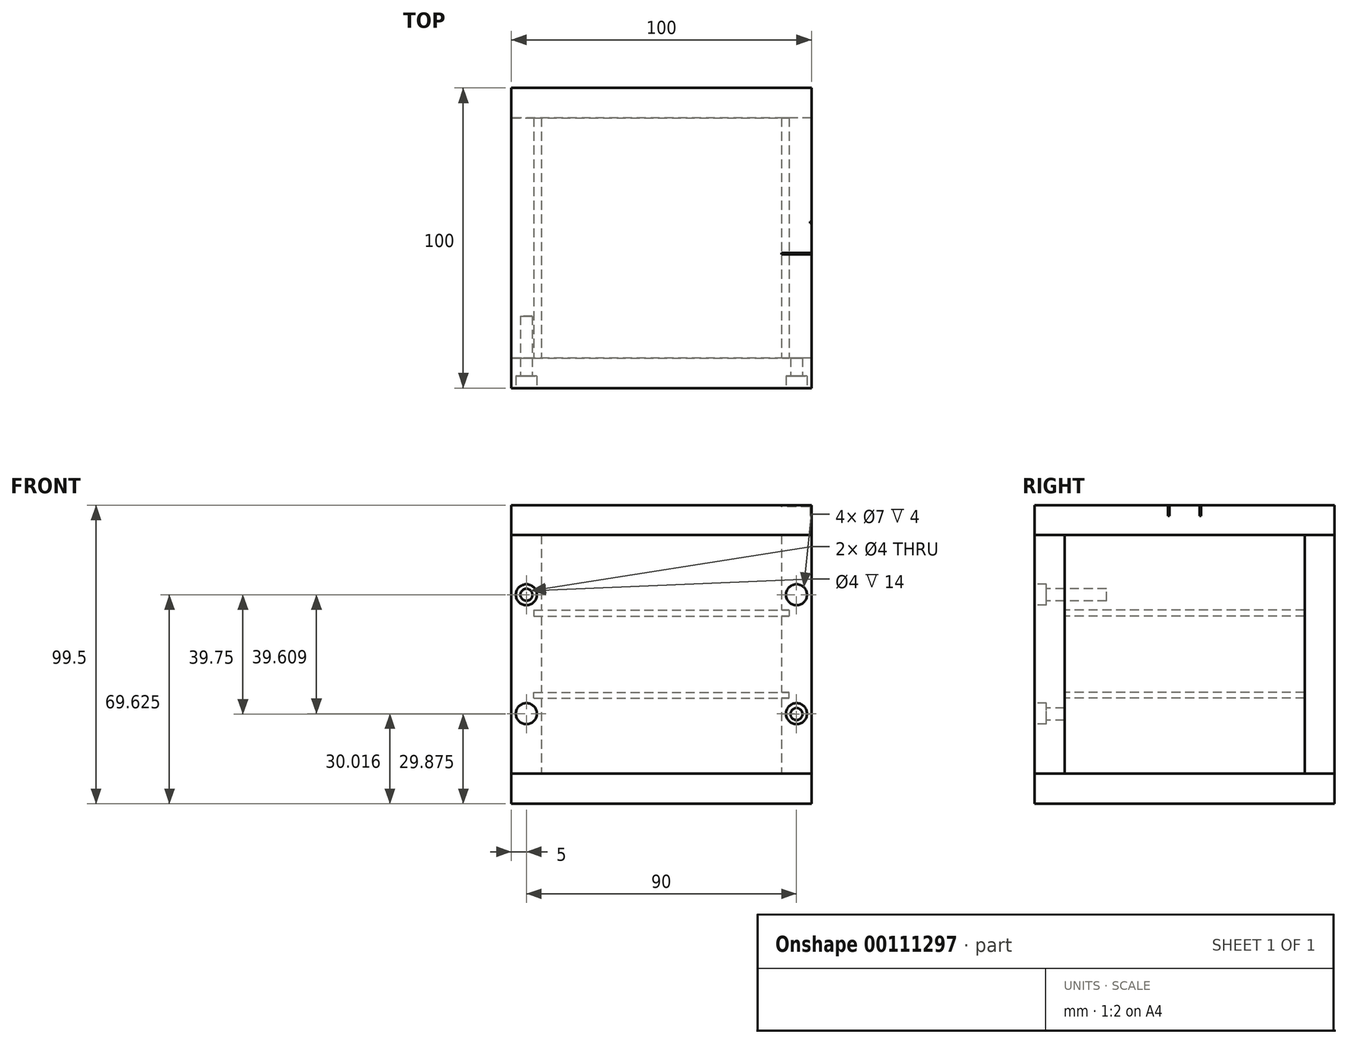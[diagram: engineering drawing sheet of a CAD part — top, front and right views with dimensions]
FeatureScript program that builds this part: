
annotation { "Feature Type Name" : "Feature", "Feature Type Description" : "" }
export const myFeature = defineFeature(function(context is Context, id is Id, definition is map)
    precondition{}
    {
        {
            var Q0;
            Q0=qCreatedBy(makeId("Top.planeOp"),FACE);
            var sketch = newSketch(context, id + "F0", { "sketchPlane" : qUnion([Q0])});
            skLineSegment(sketch, "E0.bottom", {"start": v(50, 50) * mm, "end": v(-50, 50) * mm});
            skLineSegment(sketch, "E0.top", {"start": v(50, -50) * mm, "end": v(-50, -50) * mm});
            skLineSegment(sketch, "E0.left", {"start": v(50, 50) * mm, "end": v(50, -50) * mm});
            skLineSegment(sketch, "E0.right", {"start": v(-50, 50) * mm, "end": v(-50, -50) * mm});
            skPoint(sketch, "E0.middle", {"position": v(0, 0) * mm});
            skSolve(sketch);
        }
        {
            var Q0;
            Q0=makeQuery(id+"F0.imprint","IMPRINT",FACE,{"disambiguationData":[TD([[makeQuery(id+"F0.imprint","IMPRINT",EDGE,{"derivedFrom":sQuery(id+"F0.wireOp",EDGE,"E0.bottom")}),1.0]])]});
            extrude(context, id + "F1", {"entities" : qUnion([Q0]), "depth" : 10 * mm});
        }
        {
            var Q0;
            Q0=makeQuery(id+"F1.opExtrude","CAP_FACE",FACE,{"disambiguationData":[OSD([sQuery(id+"F0.wireOp",EDGE,"E0.bottom"),sQuery(id+"F0.wireOp",EDGE,"E0.top"),sQuery(id+"F0.wireOp",EDGE,"E0.left"),sQuery(id+"F0.wireOp",EDGE,"E0.right")])],"isStart":false});
            var sketch = newSketch(context, id + "F2", { "sketchPlane" : qUnion([Q0])});
            skLineSegment(sketch, "E1.bottom", {"start": v(50, 40) * mm, "end": v(40, 40) * mm});
            skLineSegment(sketch, "E1.top", {"start": v(50, -40) * mm, "end": v(40, -40) * mm});
            skLineSegment(sketch, "E1.left", {"start": v(50, 40) * mm, "end": v(50, -40) * mm});
            skLineSegment(sketch, "E1.right", {"start": v(40, 40) * mm, "end": v(40, -40) * mm});
            skSolve(sketch);
        }
        {
            var Q0;
            Q0=makeQuery(id+"F2.imprint","IMPRINT",FACE,{"disambiguationData":[TD([[makeQuery(id+"F2.imprint","IMPRINT",EDGE,{"derivedFrom":sQuery(id+"F2.wireOp",EDGE,"E1.bottom")}),1.0]])]});
            extrude(context, id + "F3", {"entities" : qUnion([Q0]), "depth" : 79.5 * mm});
        }
        {
            var Q0;
            Q0=makeQuery(id+"F1.opExtrude","CAP_FACE",FACE,{"disambiguationData":[OSD([sQuery(id+"F0.wireOp",EDGE,"E0.bottom"),sQuery(id+"F0.wireOp",EDGE,"E0.top"),sQuery(id+"F0.wireOp",EDGE,"E0.left"),sQuery(id+"F0.wireOp",EDGE,"E0.right")])],"isStart":false});
            var sketch = newSketch(context, id + "F4", { "sketchPlane" : qUnion([Q0])});
            skLineSegment(sketch, "E2.bottom", {"start": v(-50, 40) * mm, "end": v(-40, 40) * mm});
            skLineSegment(sketch, "E2.top", {"start": v(-50, -40) * mm, "end": v(-40, -40) * mm});
            skLineSegment(sketch, "E2.left", {"start": v(-50, 40) * mm, "end": v(-50, -40) * mm});
            skLineSegment(sketch, "E2.right", {"start": v(-40, 40) * mm, "end": v(-40, -40) * mm});
            skSolve(sketch);
        }
        {
            var Q0;
            Q0=makeQuery(id+"F4.imprint","IMPRINT",FACE,{"disambiguationData":[TD([[makeQuery(id+"F4.imprint","IMPRINT",EDGE,{"derivedFrom":sQuery(id+"F4.wireOp",EDGE,"E2.bottom")}),-1.0]])]});
            extrude(context, id + "F5", {"entities" : qUnion([Q0]), "depth" : 79.5 * mm});
        }
        {
            var Q0;
            Q0=makeQuery(id+"F5.opExtrude","SWEPT_FACE",FACE,{"disambiguationData":[OSD([sQuery(id+"F4.wireOp",EDGE,"E2.top")])]});
            var sketch = newSketch(context, id + "F6", { "sketchPlane" : qUnion([Q0])});
            skPoint(sketch, "E3", {"position": v(-50, 49.75) * mm});
            skSolve(sketch);
        }
        {
            var Q0;
            Q0=makeQuery(id+"F3.opExtrude","SWEPT_FACE",FACE,{"disambiguationData":[OSD([sQuery(id+"F2.wireOp",EDGE,"E1.top")])]});
            var sketch = newSketch(context, id + "F7", { "sketchPlane" : qUnion([Q0])});
            skPoint(sketch, "E4", {"position": v(50, 49.75) * mm});
            skSolve(sketch);
        }
        {
            var Q0;
            Q0=makeQuery(id+"F3.opExtrude","SWEPT_FACE",FACE,{"disambiguationData":[OSD([sQuery(id+"F2.wireOp",EDGE,"E1.bottom")])]});
            var sketch = newSketch(context, id + "F8", { "sketchPlane" : qUnion([Q0])});
            skPoint(sketch, "E5", {"position": v(-50, 49.75) * mm});
            skSolve(sketch);
        }
        {
            var Q0;
            Q0=sQuery(id+"F6.wireOp",VERTEX,"E3");
            var Q1;
            Q1=sQuery(id+"F7.wireOp",VERTEX,"E4");
            var Q2;
            Q2=sQuery(id+"F8.wireOp",VERTEX,"E5");
            cPlane(context, id + "F9", {"entities" : qUnion([Q0, Q1, Q2]), "cplaneType" : CPlaneType.THREE_POINT, "offset" : 25 * mm, "width" : 150 * mm, "height" : 150 * mm});
        }
        {
            var Q0;
            Q0=makeQuery(id+"F1.opExtrude","SWEPT_BODY",BODY,{"disambiguationData":[OSD([sQuery(id+"F0.wireOp",EDGE,"E0.bottom"),sQuery(id+"F0.wireOp",EDGE,"E0.top"),sQuery(id+"F0.wireOp",EDGE,"E0.left"),sQuery(id+"F0.wireOp",EDGE,"E0.right")])]});
            var Q1;
            Q1=qCreatedBy(id+"F9.planeOp",FACE);
            mirror(context, id + "F10", {"entities" : qUnion([Q0]), "mirrorPlane" : qUnion([Q1])});
        }
        {
            var Q0;
            {var subQ0=sQuery(id+"F2.wireOp",EDGE,"E1.top");Q0=makeQuery(id+"F7.imprint","IMPRINT",FACE,{"disambiguationData":[TD([[makeQuery(id+"F7.imprint","IMPRINT",EDGE,{"derivedFrom":makeQuery(id+"F3.opExtrude","CAP_EDGE",EDGE,{"disambiguationData":[OSD([subQ0])],"isStart":true})}),-1.0]])]});}
            var sketch = newSketch(context, id + "F11", { "sketchPlane" : qUnion([Q0])});
            skLineSegment(sketch, "E6.bottom", {"start": v(42.5, 64.5) * mm, "end": v(37.5, 64.5) * mm});
            skLineSegment(sketch, "E6.top", {"start": v(42.5, 62.5) * mm, "end": v(37.5, 62.5) * mm});
            skLineSegment(sketch, "E6.left", {"start": v(42.5, 64.5) * mm, "end": v(42.5, 62.5) * mm});
            skLineSegment(sketch, "E6.right", {"start": v(37.5, 64.5) * mm, "end": v(37.5, 62.5) * mm});
            skLineSegment(sketch, "E7", {"start": v(0, 89.56) * mm, "end": v(0, 9.58) * mm});
            skLineSegment(sketch, "E8.MirrorCS", {"start": v(-42.5, 64.5) * mm, "end": v(-37.5, 64.5) * mm});
            skLineSegment(sketch, "E9.MirrorCS", {"start": v(-42.5, 62.5) * mm, "end": v(-37.5, 62.5) * mm});
            skLineSegment(sketch, "E10.MirrorCS", {"start": v(-42.5, 64.5) * mm, "end": v(-42.5, 62.5) * mm});
            skLineSegment(sketch, "E11.MirrorCS", {"start": v(-37.5, 64.5) * mm, "end": v(-37.5, 62.5) * mm});
            skLineSegment(sketch, "E12", {"start": v(-50.03, 49.82) * mm, "end": v(50.15, 49.82) * mm});
            skLineSegment(sketch, "E13.MirrorCS", {"start": v(42.5, 35.14) * mm, "end": v(42.5, 37.14) * mm});
            skLineSegment(sketch, "E14.MirrorCS", {"start": v(37.5, 35.14) * mm, "end": v(37.5, 37.14) * mm});
            skLineSegment(sketch, "E15.MirrorCS", {"start": v(42.5, 35.14) * mm, "end": v(37.5, 35.14) * mm});
            skLineSegment(sketch, "E16.MirrorCS", {"start": v(42.5, 37.14) * mm, "end": v(37.5, 37.14) * mm});
            skLineSegment(sketch, "E17.MirrorCS", {"start": v(-42.5, 35.14) * mm, "end": v(-37.5, 35.14) * mm});
            skLineSegment(sketch, "E18.MirrorCS", {"start": v(-37.5, 35.14) * mm, "end": v(-37.5, 37.14) * mm});
            skLineSegment(sketch, "E19.MirrorCS", {"start": v(-42.5, 35.14) * mm, "end": v(-42.5, 37.14) * mm});
            skLineSegment(sketch, "E20.MirrorCS", {"start": v(-42.5, 37.14) * mm, "end": v(-37.5, 37.14) * mm});
            skLineSegment(sketch, "E21", {"start": v(-40, 64.5) * mm, "end": v(-40, 62.5) * mm});
            skLineSegment(sketch, "E22", {"start": v(-40, 37.14) * mm, "end": v(-40, 35.14) * mm});
            skSolve(sketch);
        }
        {
            var Q0;
            {var subQ0=sQuery(id+"F11.wireOp",EDGE,"E6.left");Q0=makeQuery(id+"F11.imprint","IMPRINT",FACE,{"disambiguationData":[TD([[makeQuery(id+"F11.imprint","IMPRINT",EDGE,{"derivedFrom":subQ0}),-1.0]])]});}
            var Q1;
            {var subQ0=sQuery(id+"F11.wireOp",EDGE,"E13.MirrorCS");Q1=makeQuery(id+"F11.imprint","IMPRINT",FACE,{"disambiguationData":[TD([[makeQuery(id+"F11.imprint","IMPRINT",EDGE,{"derivedFrom":subQ0}),1.0]])]});}
            var Q2;
            {var subQ0=sQuery(id+"F11.wireOp",EDGE,"E10.MirrorCS");Q2=makeQuery(id+"F11.imprint","IMPRINT",FACE,{"disambiguationData":[TD([[makeQuery(id+"F11.imprint","IMPRINT",EDGE,{"derivedFrom":subQ0}),1.0]])]});}
            var Q3;
            {var subQ0=sQuery(id+"F11.wireOp",EDGE,"E19.MirrorCS");Q3=makeQuery(id+"F11.imprint","IMPRINT",FACE,{"disambiguationData":[TD([[makeQuery(id+"F11.imprint","IMPRINT",EDGE,{"derivedFrom":subQ0}),-1.0]])]});}
            var Q4;
            Q4=makeQuery(id+"F5.opExtrude","SWEPT_FACE",FACE,{"disambiguationData":[OSD([sQuery(id+"F4.wireOp",EDGE,"E2.bottom")])]});
            extrude(context, id + "F12", {"entities" : qUnion([Q0, Q1, Q2, Q3]), "operationType" : NewBodyOperationType.REMOVE, "endBound" : BoundingType.UP_TO_SURFACE, "oppositeDirection" : true, "endBoundEntityFace" : qUnion([Q4]), "depth" : 25 * mm});
        }
        {
            var Q0;
            Q0=makeQuery(id+"F1.opExtrude","CAP_FACE",FACE,{"disambiguationData":[OSD([sQuery(id+"F0.wireOp",EDGE,"E0.bottom"),sQuery(id+"F0.wireOp",EDGE,"E0.top"),sQuery(id+"F0.wireOp",EDGE,"E0.left"),sQuery(id+"F0.wireOp",EDGE,"E0.right")])],"isStart":false});
            var sketch = newSketch(context, id + "F13", { "sketchPlane" : qUnion([Q0])});
            skLineSegment(sketch, "E23", {"start": v(-50, -50) * mm, "end": v(50, -50) * mm});
            skLineSegment(sketch, "E24", {"start": v(50, -50) * mm, "end": v(50, -40) * mm});
            skLineSegment(sketch, "E25", {"start": v(50, -40) * mm, "end": v(-50, -40) * mm});
            skLineSegment(sketch, "E26", {"start": v(-50, -40) * mm, "end": v(-50, -50) * mm});
            skSolve(sketch);
        }
        {
            var Q0;
            Q0=makeQuery(id+"F13.imprint","IMPRINT",FACE,{"disambiguationData":[TD([[makeQuery(id+"F13.imprint","IMPRINT",EDGE,{"derivedFrom":sQuery(id+"F13.wireOp",EDGE,"E23")}),-1.0]])]});
            extrude(context, id + "F14", {"entities" : qUnion([Q0]), "depth" : 79.5 * mm});
        }
        {
            var Q0;
            Q0=makeQuery(id+"F14.opExtrude","SWEPT_BODY",BODY,{"disambiguationData":[OSD([sQuery(id+"F13.wireOp",EDGE,"E23"),sQuery(id+"F13.wireOp",EDGE,"E24"),sQuery(id+"F13.wireOp",EDGE,"E25"),sQuery(id+"F13.wireOp",EDGE,"E26")])]});
            var Q1;
            Q1=qCreatedBy(makeId("Front.planeOp"),FACE);
            mirror(context, id + "F15", {"entities" : qUnion([Q0]), "mirrorPlane" : qUnion([Q1])});
        }
        {
            var Q0;
            {var subQ0=sQuery(id+"F4.wireOp",EDGE,"E2.top");Q0=makeQuery(id+"F6.imprint","IMPRINT",FACE,{"disambiguationData":[TD([[makeQuery(id+"F6.imprint","IMPRINT",EDGE,{"derivedFrom":makeQuery(id+"F5.opExtrude","CAP_EDGE",EDGE,{"disambiguationData":[OSD([subQ0])],"isStart":true})}),1.0]])]});}
            var sketch = newSketch(context, id + "F16", { "sketchPlane" : qUnion([Q0])});
            skPoint(sketch, "E27", {"position": v(-45, 89.5) * mm});
            skPoint(sketch, "E28.0.1.0", {"position": v(-45, 69.62) * mm});
            skPoint(sketch, "E29.0.0.3", {"position": v(-45, 29.87) * mm});
            skCircle(sketch, "E30", {"center": v(-45, 69.62) * mm, "radius": 2 * mm});
            skCircle(sketch, "E31", {"center": v(-45, 29.87) * mm, "radius": 2 * mm});
            skCircle(sketch, "E32.MirrorC", {"center": v(45, 69.62) * mm, "radius": 2 * mm});
            skCircle(sketch, "E33.MirrorC", {"center": v(45, 29.87) * mm, "radius": 2 * mm});
            skSolve(sketch);
        }
        {
            var Q0;
            Q0=makeQuery(id+"F16.imprint","IMPRINT",FACE,{"disambiguationData":[TD([[makeQuery(id+"F16.imprint","IMPRINT",EDGE,{"derivedFrom":sQuery(id+"F16.wireOp",EDGE,"E30")}),1.0]])]});
            var Q1;
            Q1=makeQuery(id+"F16.imprint","IMPRINT",FACE,{"disambiguationData":[TD([[makeQuery(id+"F16.imprint","IMPRINT",EDGE,{"derivedFrom":sQuery(id+"F16.wireOp",EDGE,"E32.MirrorC")}),-1.0]])]});
            extrude(context, id + "F17", {"entities" : qUnion([Q0, Q1]), "operationType" : NewBodyOperationType.REMOVE, "oppositeDirection" : true, "depth" : 14 * mm});
        }
        {
            var Q0;
            Q0=sQuery(id+"F11.wireOp",EDGE,"E12");
            cPlane(context, id + "F18", {"entities" : qUnion([Q0]), "cplaneType" : CPlaneType.LINE_ANGLE, "offset" : 25 * mm, "angle" : 90 * degree, "width" : 150 * mm, "height" : 150 * mm});
        }
        {
            var Q0;
            Q0=makeQuery(id+"F3.opExtrude","SWEPT_FACE",FACE,{"disambiguationData":[OSD([sQuery(id+"F2.wireOp",EDGE,"E1.left")])]});
            var sketch = newSketch(context, id + "F19", { "sketchPlane" : qUnion([Q0])});
            skLineSegment(sketch, "E34", {"start": v(-40, 89.5) * mm, "end": v(40, 89.5) * mm});
            skLineSegment(sketch, "E35", {"start": v(40, 10) * mm, "end": v(-40, 10) * mm});
            skLineSegment(sketch, "E36", {"start": v(0, 89.5) * mm, "end": v(0, 10) * mm});
            skSolve(sketch);
        }
        {
            var Q0;
            Q0=sQuery(id+"F19.wireOp",EDGE,"E36");
            cPlane(context, id + "F20", {"entities" : qUnion([Q0]), "cplaneType" : CPlaneType.LINE_ANGLE, "offset" : 25 * mm, "angle" : 90 * degree, "width" : 150 * mm, "height" : 150 * mm});
        }
        {
            var Q0;
            Q0=makeQuery(id+"F14.opExtrude","SWEPT_FACE",FACE,{"disambiguationData":[OSD([sQuery(id+"F13.wireOp",EDGE,"E23")])]});
            var sketch = newSketch(context, id + "F21", { "sketchPlane" : qUnion([Q0])});
            skCircle(sketch, "E37", {"center": v(-45, 69.62) * mm, "radius": 3.5 * mm});
            skCircle(sketch, "E38", {"center": v(-45, 30.02) * mm, "radius": 3.5 * mm});
            skCircle(sketch, "E39", {"center": v(45, 69.62) * mm, "radius": 3.5 * mm});
            skCircle(sketch, "E40", {"center": v(45, 30.02) * mm, "radius": 3.5 * mm});
            skSolve(sketch);
        }
        {
            var Q0;
            Q0=makeQuery(id+"F21.imprint","IMPRINT",FACE,{"disambiguationData":[TD([[makeQuery(id+"F21.imprint","IMPRINT",EDGE,{"derivedFrom":sQuery(id+"F21.wireOp",EDGE,"E37")}),1.0]])]});
            var Q1;
            Q1=makeQuery(id+"F21.imprint","IMPRINT",FACE,{"disambiguationData":[TD([[makeQuery(id+"F21.imprint","IMPRINT",EDGE,{"derivedFrom":sQuery(id+"F21.wireOp",EDGE,"E38")}),1.0]])]});
            var Q2;
            Q2=makeQuery(id+"F21.imprint","IMPRINT",FACE,{"disambiguationData":[TD([[makeQuery(id+"F21.imprint","IMPRINT",EDGE,{"derivedFrom":sQuery(id+"F21.wireOp",EDGE,"E39")}),1.0]])]});
            var Q3;
            Q3=makeQuery(id+"F21.imprint","IMPRINT",FACE,{"disambiguationData":[TD([[makeQuery(id+"F21.imprint","IMPRINT",EDGE,{"derivedFrom":sQuery(id+"F21.wireOp",EDGE,"E40")}),1.0]])]});
            extrude(context, id + "F22", {"entities" : qUnion([Q0, Q1, Q2, Q3]), "operationType" : NewBodyOperationType.REMOVE, "oppositeDirection" : true, "depth" : 4 * mm});
        }
        {
            var Q0;
            Q0=makeQuery(id+"F22.boolean.opBoolean","COPY",FACE,{"derivedFrom":makeQuery(id+"F22.opExtrude","CAP_FACE",FACE,{"disambiguationData":[OSD([sQuery(id+"F21.wireOp",EDGE,"E37")])],"isStart":false})});
            var sketch = newSketch(context, id + "F23", { "sketchPlane" : qUnion([Q0])});
            skCircle(sketch, "E41", {"center": v(-45, 69.62) * mm, "radius": 2 * mm});
            skCircle(sketch, "E42.0", {"center": v(-45, 69.62) * mm, "radius": 3.5 * mm});
            skCircle(sketch, "E43.MirrorC", {"center": v(-45, 29.88) * mm, "radius": 2 * mm});
            skCircle(sketch, "E44.MirrorC", {"center": v(45, 69.62) * mm, "radius": 2 * mm});
            skCircle(sketch, "E45.MirrorC", {"center": v(45, 29.88) * mm, "radius": 2 * mm});
            skSolve(sketch);
        }
        {
            var Q0;
            Q0=makeQuery(id+"F5.opExtrude","SWEPT_FACE",FACE,{"disambiguationData":[OSD([sQuery(id+"F4.wireOp",EDGE,"E2.top")])]});
            var sketch = newSketch(context, id + "F24", { "sketchPlane" : qUnion([Q0])});
            skPoint(sketch, "E46.0", {"position": v(-42.5, 64.5) * mm});
            skPoint(sketch, "E47.0", {"position": v(42.5, 62.5) * mm});
            skLineSegment(sketch, "E48.bottom", {"start": v(-42.5, 64.5) * mm, "end": v(42.5, 64.5) * mm});
            skLineSegment(sketch, "E48.top", {"start": v(-42.5, 62.5) * mm, "end": v(42.5, 62.5) * mm});
            skLineSegment(sketch, "E48.left", {"start": v(-42.5, 64.5) * mm, "end": v(-42.5, 62.5) * mm});
            skLineSegment(sketch, "E48.right", {"start": v(42.5, 64.5) * mm, "end": v(42.5, 62.5) * mm});
            skPoint(sketch, "E49.0", {"position": v(-42.5, 37.14) * mm});
            skPoint(sketch, "E50.0", {"position": v(42.5, 35.14) * mm});
            skSolve(sketch);
        }
        {
            var Q0;
            {var subQ0=sQuery(id+"F24.wireOp",EDGE,"E48.left");Q0=makeQuery(id+"F24.imprint","IMPRINT",FACE,{"disambiguationData":[TD([[makeQuery(id+"F24.imprint","IMPRINT",EDGE,{"derivedFrom":subQ0}),1.0]])]});}
            extrude(context, id + "F25", {"entities" : qUnion([Q0]), "endBound" : BoundingType.UP_TO_NEXT, "oppositeDirection" : true, "depth" : 25 * mm});
        }
        {
            var Q0;
            Q0=makeQuery(id+"F25.opExtrude","SWEPT_BODY",BODY,{"disambiguationData":[OSD([sQuery(id+"F24.wireOp",EDGE,"E48.bottom"),sQuery(id+"F24.wireOp",EDGE,"E48.top"),sQuery(id+"F24.wireOp",EDGE,"E48.left"),sQuery(id+"F24.wireOp",EDGE,"E48.right")])]});
            var Q1;
            Q1=makeQuery(id+"F12.boolean.opBoolean","COPY",VERTEX,{"derivedFrom":makeQuery(id+"F12.opExtrude","CAP_VERTEX",VERTEX,{"disambiguationData":[OSD([sQuery(id+"F11.wireOp",EDGE,"E8.MirrorCS"),sQuery(id+"F11.wireOp",EDGE,"E10.MirrorCS")])],"isStart":true})});
            var Q2;
            Q2=makeQuery(id+"F12.boolean.opBoolean","COPY",VERTEX,{"derivedFrom":makeQuery(id+"F12.opExtrude","CAP_VERTEX",VERTEX,{"disambiguationData":[OSD([sQuery(id+"F11.wireOp",EDGE,"E19.MirrorCS"),sQuery(id+"F11.wireOp",EDGE,"E20.MirrorCS")])],"isStart":true})});
            transform(context, id + "F26", {"entities" : qUnion([Q0]), "transformType" : TransformType.TRANSLATION_ENTITY, "oppositeDirectionEntity" : false, "transformLine" : qUnion([Q1, Q2]), "makeCopy" : true});
        }
        {
            var Q0;
            Q0=makeQuery(id+"F10.opPattern","COPY",FACE,{"derivedFrom":makeQuery(id+"F1.opExtrude","CAP_FACE",FACE,{"disambiguationData":[OSD([sQuery(id+"F0.wireOp",EDGE,"E0.bottom"),sQuery(id+"F0.wireOp",EDGE,"E0.top"),sQuery(id+"F0.wireOp",EDGE,"E0.left"),sQuery(id+"F0.wireOp",EDGE,"E0.right")])],"isStart":true}),"instanceName":"1"});
            var sketch = newSketch(context, id + "F27", { "sketchPlane" : qUnion([Q0])});
            skLineSegment(sketch, "E51", {"start": v(50, 0) * mm, "end": v(40, 0) * mm});
            skPoint(sketch, "E51.endSnap0", {"position": v(50, 0) * mm});
            skLineSegment(sketch, "E52.0", {"start": v(50, 5) * mm, "end": v(40, 5) * mm});
            skLineSegment(sketch, "E53.bottom", {"start": v(40, 5) * mm, "end": v(50, 5) * mm});
            skLineSegment(sketch, "E53.top", {"start": v(40, 5.5) * mm, "end": v(50, 5.5) * mm});
            skLineSegment(sketch, "E53.left", {"start": v(40, 5) * mm, "end": v(40, 5.5) * mm});
            skLineSegment(sketch, "E53.right", {"start": v(50, 5) * mm, "end": v(50, 5.5) * mm});
            skLineSegment(sketch, "E54.MirrorCS", {"start": v(50, -5) * mm, "end": v(50, -5.5) * mm});
            skLineSegment(sketch, "E55.MirrorCS", {"start": v(40, -5) * mm, "end": v(40, -5.5) * mm});
            skLineSegment(sketch, "E56.MirrorCS", {"start": v(50, -5) * mm, "end": v(40, -5) * mm});
            skLineSegment(sketch, "E57.MirrorCS", {"start": v(40, -5.5) * mm, "end": v(50, -5.5) * mm});
            skLineSegment(sketch, "E58.MirrorCS", {"start": v(40, -5) * mm, "end": v(50, -5) * mm});
            skSolve(sketch);
        }
        {
            var Q0;
            Q0=makeQuery(id+"F27.imprint","IMPRINT",FACE,{"disambiguationData":[TD([[makeQuery(id+"F27.imprint","IMPRINT",EDGE,{"derivedFrom":sQuery(id+"F27.wireOp",EDGE,"E53.bottom")}),1.0]])]});
            var Q1;
            Q1=makeQuery(id+"F27.imprint","IMPRINT",FACE,{"disambiguationData":[TD([[makeQuery(id+"F27.imprint","IMPRINT",EDGE,{"derivedFrom":sQuery(id+"F27.wireOp",EDGE,"E54.MirrorCS")}),-1.0]])]});
            extrude(context, id + "F28", {"entities" : qUnion([Q0, Q1]), "operationType" : NewBodyOperationType.REMOVE, "oppositeDirection" : true, "depth" : 0.5 * mm});
        }
        {
            var Q0;
            Q0=makeQuery(id+"F10.opPattern","COPY",FACE,{"derivedFrom":makeQuery(id+"F1.opExtrude","SWEPT_FACE",FACE,{"disambiguationData":[OSD([sQuery(id+"F0.wireOp",EDGE,"E0.left")])]}),"instanceName":"1"});
            var sketch = newSketch(context, id + "F29", { "sketchPlane" : qUnion([Q0])});
            skLineSegment(sketch, "E59.bottom", {"start": v(-5.5, 99.5) * mm, "end": v(-5, 99.5) * mm});
            skLineSegment(sketch, "E59.top", {"start": v(-5.5, 95.84) * mm, "end": v(-5, 95.84) * mm});
            skLineSegment(sketch, "E59.left", {"start": v(-5.5, 99.5) * mm, "end": v(-5.5, 95.84) * mm});
            skLineSegment(sketch, "E59.right", {"start": v(-5, 99.5) * mm, "end": v(-5, 95.84) * mm});
            skLineSegment(sketch, "E60", {"start": v(0, 99.5) * mm, "end": v(0, 95.34) * mm});
            skPoint(sketch, "E60.endSnap0", {"position": v(0, 99.5) * mm});
            skLineSegment(sketch, "E61.MirrorCS", {"start": v(5, 99.5) * mm, "end": v(5, 95.84) * mm});
            skLineSegment(sketch, "E62.MirrorCS", {"start": v(5.5, 95.84) * mm, "end": v(5, 95.84) * mm});
            skLineSegment(sketch, "E63.MirrorCS", {"start": v(5.5, 99.5) * mm, "end": v(5.5, 95.84) * mm});
            skLineSegment(sketch, "E64.MirrorCS", {"start": v(5.5, 99.5) * mm, "end": v(5, 99.5) * mm});
            skSolve(sketch);
        }
        {
            var Q0;
            {var subQ0=sQuery(id+"F29.wireOp",EDGE,"E59.top");Q0=makeQuery(id+"F29.imprint","IMPRINT",FACE,{"disambiguationData":[TD([[makeQuery(id+"F29.imprint","IMPRINT",EDGE,{"derivedFrom":subQ0}),1.0]])]});}
            var Q1;
            {var subQ2=sQuery(id+"F29.wireOp",EDGE,"E62.MirrorCS");Q1=makeQuery(id+"F29.imprint","IMPRINT",FACE,{"disambiguationData":[TD([[makeQuery(id+"F29.imprint","IMPRINT",EDGE,{"derivedFrom":subQ2}),-1.0]])]});}
            extrude(context, id + "F30", {"entities" : qUnion([Q0, Q1]), "operationType" : NewBodyOperationType.REMOVE, "oppositeDirection" : true, "depth" : 0.5 * mm});
        }
        {
            var Q0;
            Q0=makeQuery(id+"F23.imprint","IMPRINT",FACE,{"disambiguationData":[TD([[makeQuery(id+"F23.imprint","IMPRINT",EDGE,{"derivedFrom":sQuery(id+"F23.wireOp",EDGE,"E41")}),1.0]])]});
            var Q1;
            Q1=makeQuery(id+"F23.imprint","IMPRINT",FACE,{"disambiguationData":[TD([[makeQuery(id+"F23.imprint","IMPRINT",EDGE,{"derivedFrom":sQuery(id+"F23.wireOp",EDGE,"E43.MirrorC")}),-1.0]])]});
            var Q2;
            Q2=makeQuery(id+"F23.imprint","IMPRINT",FACE,{"disambiguationData":[TD([[makeQuery(id+"F23.imprint","IMPRINT",EDGE,{"derivedFrom":sQuery(id+"F23.wireOp",EDGE,"E44.MirrorC")}),-1.0]])]});
            var Q3;
            Q3=makeQuery(id+"F23.imprint","IMPRINT",FACE,{"disambiguationData":[TD([[makeQuery(id+"F23.imprint","IMPRINT",EDGE,{"derivedFrom":sQuery(id+"F23.wireOp",EDGE,"E45.MirrorC")}),1.0]])]});
            extrude(context, id + "F31", {"entities" : qUnion([Q0, Q1, Q2, Q3]), "operationType" : NewBodyOperationType.REMOVE, "oppositeDirection" : true, "depth" : 6 * mm});
        }
    });
